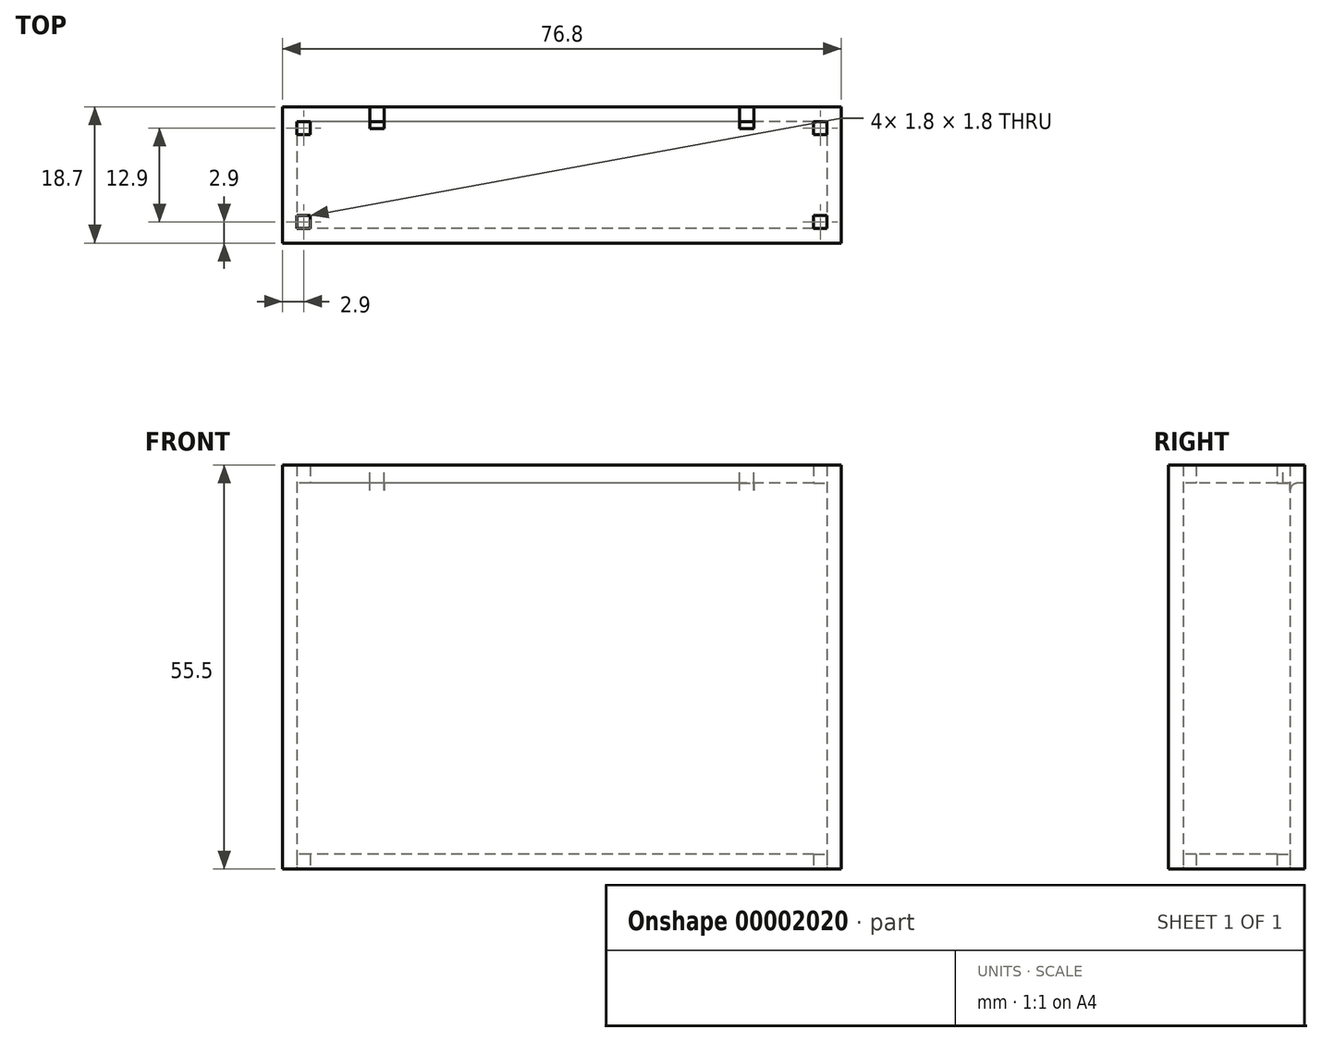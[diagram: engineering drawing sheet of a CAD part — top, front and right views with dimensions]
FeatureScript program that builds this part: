
annotation { "Feature Type Name" : "Feature", "Feature Type Description" : "" }
export const myFeature = defineFeature(function(context is Context, id is Id, definition is map)
    precondition{}
    {
        {
            var Q0;
            Q0=qCreatedBy(makeId("Top.planeOp"),FACE);
            var sketch = newSketch(context, id + "F0", { "sketchPlane" : qUnion([Q0])});
            skLineSegment(sketch, "E0.rect.bottom", {"start": v(36.4, 7.35) * mm, "end": v(-36.4, 7.35) * mm});
            skLineSegment(sketch, "E0.rect.top", {"start": v(36.4, -7.35) * mm, "end": v(-36.4, -7.35) * mm});
            skLineSegment(sketch, "E0.rect.left", {"start": v(36.4, 7.35) * mm, "end": v(36.4, -7.35) * mm});
            skLineSegment(sketch, "E0.rect.right", {"start": v(-36.4, 7.35) * mm, "end": v(-36.4, -7.35) * mm});
            skPoint(sketch, "E0.rect.middle", {"position": v(0, 0) * mm});
            skCircle(sketch, "E1", {"center": v(-29.15, 0.1) * mm, "radius": 7.25 * mm, "construction": true});
            skCircle(sketch, "E2", {"center": v(-14.65, -0.1) * mm, "radius": 7.25 * mm, "construction": true});
            skCircle(sketch, "E3", {"center": v(-0.15, 0.1) * mm, "radius": 7.25 * mm, "construction": true});
            skCircle(sketch, "E4", {"center": v(14.35, -0.1) * mm, "radius": 7.25 * mm, "construction": true});
            skCircle(sketch, "E5", {"center": v(28.84, 0.1) * mm, "radius": 7.25 * mm, "construction": true});
            skLineSegment(sketch, "E6.rect.bottom", {"start": v(38.4, 9.35) * mm, "end": v(-38.4, 9.35) * mm});
            skLineSegment(sketch, "E6.rect.top", {"start": v(38.4, -9.35) * mm, "end": v(-38.4, -9.35) * mm});
            skLineSegment(sketch, "E6.rect.left", {"start": v(38.4, 9.35) * mm, "end": v(38.4, -9.35) * mm});
            skLineSegment(sketch, "E6.rect.right", {"start": v(-38.4, 9.35) * mm, "end": v(-38.4, -9.35) * mm});
            skSolve(sketch);
        }
        {
            var Q0;
            Q0=makeQuery(id+"F0.imprint","IMPRINT",FACE,{"disambiguationData":[TD([[makeQuery(id+"F0.imprint","IMPRINT",EDGE,{"derivedFrom":sQuery(id+"F0.wireOp",EDGE,"E0.rect.bottom")}),-1.0]])]});
            extrude(context, id + "F1", {"entities" : qUnion([Q0]), "depth" : 54.5 * mm});
        }
        {
            var Q0;
            Q0=makeQuery(id+"F0.imprint","IMPRINT",FACE,{"disambiguationData":[TD([[makeQuery(id+"F0.imprint","IMPRINT",EDGE,{"derivedFrom":sQuery(id+"F0.wireOp",EDGE,"E0.rect.bottom")}),1.0]])]});
            extrude(context, id + "F2", {"entities" : qUnion([Q0]), "operationType" : NewBodyOperationType.ADD, "depth" : 2 * mm});
        }
        {
            var Q0;
            Q0=makeQuery(id+"F1.opExtrude","CAP_FACE",FACE,{"disambiguationData":[OSD([sQuery(id+"F0.wireOp",EDGE,"E0.rect.bottom"),sQuery(id+"F0.wireOp",EDGE,"E0.rect.top"),sQuery(id+"F0.wireOp",EDGE,"E0.rect.left"),sQuery(id+"F0.wireOp",EDGE,"E0.rect.right"),sQuery(id+"F0.wireOp",EDGE,"E6.rect.bottom"),sQuery(id+"F0.wireOp",EDGE,"E6.rect.top"),sQuery(id+"F0.wireOp",EDGE,"E6.rect.left"),sQuery(id+"F0.wireOp",EDGE,"E6.rect.right")])],"isStart":false});
            var sketch = newSketch(context, id + "F3", { "sketchPlane" : qUnion([Q0])});
            skLineSegment(sketch, "E7.0", {"start": v(38.4, 9.35) * mm, "end": v(-38.4, 9.35) * mm});
            skLineSegment(sketch, "E7.1", {"start": v(-38.4, 9.35) * mm, "end": v(-38.4, -9.35) * mm});
            skLineSegment(sketch, "E8.0", {"start": v(36.4, 7.35) * mm, "end": v(-36.4, 7.35) * mm});
            skLineSegment(sketch, "E8.1", {"start": v(-36.4, 7.35) * mm, "end": v(-36.4, -7.35) * mm});
            skLineSegment(sketch, "E8.2", {"start": v(36.4, -7.35) * mm, "end": v(-36.4, -7.35) * mm});
            skLineSegment(sketch, "E8.3", {"start": v(36.4, 7.35) * mm, "end": v(36.4, -7.35) * mm});
            skLineSegment(sketch, "E8.4", {"start": v(38.4, 9.35) * mm, "end": v(38.4, -9.35) * mm});
            skLineSegment(sketch, "E8.5", {"start": v(38.4, -9.35) * mm, "end": v(-38.4, -9.35) * mm});
            skSolve(sketch);
        }
        {
            var Q0;
            Q0=makeQuery(id+"F3.imprint","IMPRINT",FACE,{"disambiguationData":[TD([[makeQuery(id+"F3.imprint","IMPRINT",EDGE,{"derivedFrom":sQuery(id+"F3.wireOp",EDGE,"E8.0")}),1.0]])]});
            extrude(context, id + "F4", {"entities" : qUnion([Q0]), "oppositeDirection" : true, "depth" : 1.5 * mm});
        }
        {
            var Q0;
            Q0=makeQuery(id+"F1.opExtrude","CAP_FACE",FACE,{"disambiguationData":[OSD([sQuery(id+"F0.wireOp",EDGE,"E0.rect.bottom"),sQuery(id+"F0.wireOp",EDGE,"E0.rect.top"),sQuery(id+"F0.wireOp",EDGE,"E0.rect.left"),sQuery(id+"F0.wireOp",EDGE,"E0.rect.right"),sQuery(id+"F0.wireOp",EDGE,"E6.rect.bottom"),sQuery(id+"F0.wireOp",EDGE,"E6.rect.top"),sQuery(id+"F0.wireOp",EDGE,"E6.rect.left"),sQuery(id+"F0.wireOp",EDGE,"E6.rect.right")])],"isStart":false});
            var Q1;
            Q1=makeQuery(id+"F4.opExtrude","CAP_FACE",FACE,{"disambiguationData":[OSD([sQuery(id+"F3.wireOp",EDGE,"E8.0"),sQuery(id+"F3.wireOp",EDGE,"E8.1"),sQuery(id+"F3.wireOp",EDGE,"E8.2"),sQuery(id+"F3.wireOp",EDGE,"E8.3")])],"isStart":true});
            extrude(context, id + "F5", {"entities" : qUnion([Q0, Q1]), "operationType" : NewBodyOperationType.ADD, "depth" : 1 * mm});
        }
        {
            var Q0;
            Q0=makeQuery(id+"F4.opExtrude","CAP_FACE",FACE,{"disambiguationData":[OSD([sQuery(id+"F3.wireOp",EDGE,"E8.0"),sQuery(id+"F3.wireOp",EDGE,"E8.1"),sQuery(id+"F3.wireOp",EDGE,"E8.2"),sQuery(id+"F3.wireOp",EDGE,"E8.3")])],"isStart":false});
            var sketch = newSketch(context, id + "F6", { "sketchPlane" : qUnion([Q0])});
            skLineSegment(sketch, "E9.bottom", {"start": v(36.4, -7.35) * mm, "end": v(34.6, -7.35) * mm});
            skLineSegment(sketch, "E9.top", {"start": v(36.4, -5.55) * mm, "end": v(34.6, -5.55) * mm});
            skLineSegment(sketch, "E9.left", {"start": v(36.4, -7.35) * mm, "end": v(36.4, -5.55) * mm});
            skLineSegment(sketch, "E9.right", {"start": v(34.6, -7.35) * mm, "end": v(34.6, -5.55) * mm});
            skLineSegment(sketch, "E10.bottom", {"start": v(36.4, 7.35) * mm, "end": v(34.6, 7.35) * mm});
            skLineSegment(sketch, "E10.top", {"start": v(36.4, 5.55) * mm, "end": v(34.6, 5.55) * mm});
            skLineSegment(sketch, "E10.left", {"start": v(36.4, 7.35) * mm, "end": v(36.4, 5.55) * mm});
            skLineSegment(sketch, "E10.right", {"start": v(34.6, 7.35) * mm, "end": v(34.6, 5.55) * mm});
            skLineSegment(sketch, "E11.bottom", {"start": v(-36.4, -7.35) * mm, "end": v(-34.6, -7.35) * mm});
            skLineSegment(sketch, "E11.top", {"start": v(-36.4, -5.55) * mm, "end": v(-34.6, -5.55) * mm});
            skLineSegment(sketch, "E11.left", {"start": v(-36.4, -7.35) * mm, "end": v(-36.4, -5.55) * mm});
            skLineSegment(sketch, "E11.right", {"start": v(-34.6, -7.35) * mm, "end": v(-34.6, -5.55) * mm});
            skLineSegment(sketch, "E12.bottom", {"start": v(-36.4, 7.35) * mm, "end": v(-34.6, 7.35) * mm});
            skLineSegment(sketch, "E12.top", {"start": v(-36.4, 5.55) * mm, "end": v(-34.6, 5.55) * mm});
            skLineSegment(sketch, "E12.left", {"start": v(-36.4, 7.35) * mm, "end": v(-36.4, 5.55) * mm});
            skLineSegment(sketch, "E12.right", {"start": v(-34.6, 7.35) * mm, "end": v(-34.6, 5.55) * mm});
            skSolve(sketch);
        }
        {
            var Q0;
            Q0=makeQuery(id+"F6.imprint","IMPRINT",FACE,{"disambiguationData":[TD([[makeQuery(id+"F6.imprint","IMPRINT",EDGE,{"derivedFrom":sQuery(id+"F6.wireOp",EDGE,"E9.bottom")}),-1.0]])]});
            var Q1;
            Q1=makeQuery(id+"F6.imprint","IMPRINT",FACE,{"disambiguationData":[TD([[makeQuery(id+"F6.imprint","IMPRINT",EDGE,{"derivedFrom":sQuery(id+"F6.wireOp",EDGE,"E10.bottom")}),1.0]])]});
            var Q2;
            Q2=makeQuery(id+"F6.imprint","IMPRINT",FACE,{"disambiguationData":[TD([[makeQuery(id+"F6.imprint","IMPRINT",EDGE,{"derivedFrom":sQuery(id+"F6.wireOp",EDGE,"E11.bottom")}),-1.0]])]});
            var Q3;
            Q3=makeQuery(id+"F6.imprint","IMPRINT",FACE,{"disambiguationData":[TD([[makeQuery(id+"F6.imprint","IMPRINT",EDGE,{"derivedFrom":sQuery(id+"F6.wireOp",EDGE,"E12.bottom")}),1.0]])]});
            extrude(context, id + "F7", {"entities" : qUnion([Q0, Q1, Q2, Q3]), "operationType" : NewBodyOperationType.REMOVE, "endBound" : BoundingType.SYMMETRIC, "oppositeDirection" : true, "depth" : 300 * mm});
        }
        {
            var Q0;
            Q0=makeQuery(id+"F5.boolean.opBoolean","MERGE",FACE,{"derivedFrom":[makeQuery(id+"F5.opExtrude","CAP_FACE",FACE,{"disambiguationData":[OSD([sQuery(id+"F0.wireOp",EDGE,"E0.rect.bottom"),sQuery(id+"F0.wireOp",EDGE,"E0.rect.top"),sQuery(id+"F0.wireOp",EDGE,"E0.rect.left"),sQuery(id+"F0.wireOp",EDGE,"E0.rect.right"),sQuery(id+"F0.wireOp",EDGE,"E6.rect.bottom"),sQuery(id+"F0.wireOp",EDGE,"E6.rect.top"),sQuery(id+"F0.wireOp",EDGE,"E6.rect.left"),sQuery(id+"F0.wireOp",EDGE,"E6.rect.right")])],"isStart":false}),makeQuery(id+"F5.opExtrude","CAP_FACE",FACE,{"disambiguationData":[OSD([sQuery(id+"F3.wireOp",EDGE,"E8.0"),sQuery(id+"F3.wireOp",EDGE,"E8.1"),sQuery(id+"F3.wireOp",EDGE,"E8.2"),sQuery(id+"F3.wireOp",EDGE,"E8.3")])],"isStart":false})]});
            var sketch = newSketch(context, id + "F8", { "sketchPlane" : qUnion([Q0])});
            skLineSegment(sketch, "E13.bottom", {"start": v(-24.4, 9.35) * mm, "end": v(-26.4, 9.35) * mm});
            skLineSegment(sketch, "E13.top", {"start": v(-24.4, 6.35) * mm, "end": v(-26.4, 6.35) * mm});
            skLineSegment(sketch, "E13.left", {"start": v(-24.4, 9.35) * mm, "end": v(-24.4, 6.35) * mm});
            skLineSegment(sketch, "E13.right", {"start": v(-26.4, 9.35) * mm, "end": v(-26.4, 6.35) * mm});
            skLineSegment(sketch, "E14.bottom", {"start": v(24.4, 9.35) * mm, "end": v(26.4, 9.35) * mm});
            skLineSegment(sketch, "E14.top", {"start": v(24.4, 6.35) * mm, "end": v(26.4, 6.35) * mm});
            skLineSegment(sketch, "E14.left", {"start": v(24.4, 9.35) * mm, "end": v(24.4, 6.35) * mm});
            skLineSegment(sketch, "E14.right", {"start": v(26.4, 9.35) * mm, "end": v(26.4, 6.35) * mm});
            skPoint(sketch, "E15", {"position": v(0, 9.35) * mm});
            skSolve(sketch);
        }
        {
            var Q0;
            Q0=makeQuery(id+"F8.imprint","IMPRINT",FACE,{"disambiguationData":[TD([[makeQuery(id+"F8.imprint","IMPRINT",EDGE,{"derivedFrom":sQuery(id+"F8.wireOp",EDGE,"E13.bottom")}),1.0]])]});
            var Q1;
            Q1=makeQuery(id+"F8.imprint","IMPRINT",FACE,{"disambiguationData":[TD([[makeQuery(id+"F8.imprint","IMPRINT",EDGE,{"derivedFrom":sQuery(id+"F8.wireOp",EDGE,"E14.bottom")}),1.0]])]});
            extrude(context, id + "F9", {"entities" : qUnion([Q0, Q1]), "operationType" : NewBodyOperationType.REMOVE, "oppositeDirection" : true, "depth" : 2.5 * mm});
        }
        {
            var Q0;
            Q0=makeQuery(id+"F9.boolean.opBoolean","INTERSECT",EDGE,{"derivedFrom":[makeQuery(id+"F7.boolean.opBoolean","MERGE",FACE,{"derivedFrom":[makeQuery(id+"F1.opExtrude","SWEPT_FACE",FACE,{"disambiguationData":[OSD([sQuery(id+"F0.wireOp",EDGE,"E0.rect.bottom")])]}),makeQuery(id+"F7.opExtrude","SWEPT_FACE",FACE,{"disambiguationData":[OSD([sQuery(id+"F6.wireOp",EDGE,"E9.bottom")])]}),makeQuery(id+"F7.opExtrude","SWEPT_FACE",FACE,{"disambiguationData":[OSD([sQuery(id+"F6.wireOp",EDGE,"E11.bottom")])]})]}),makeQuery(id+"F9.opExtrude","CAP_FACE",FACE,{"disambiguationData":[OSD([sQuery(id+"F8.wireOp",EDGE,"E13.bottom"),sQuery(id+"F8.wireOp",EDGE,"E13.top"),sQuery(id+"F8.wireOp",EDGE,"E13.left"),sQuery(id+"F8.wireOp",EDGE,"E13.right")])],"isStart":false})]});
            var Q1;
            Q1=makeQuery(id+"F9.boolean.opBoolean","COPY",EDGE,{"derivedFrom":makeQuery(id+"F9.opExtrude","CAP_EDGE",EDGE,{"disambiguationData":[OSD([sQuery(id+"F8.wireOp",EDGE,"E13.top")])],"isStart":false})});
            var Q2;
            Q2=makeQuery(id+"F9.boolean.opBoolean","COPY",EDGE,{"derivedFrom":makeQuery(id+"F9.opExtrude","CAP_EDGE",EDGE,{"disambiguationData":[OSD([sQuery(id+"F8.wireOp",EDGE,"E14.top")])],"isStart":false})});
            var Q3;
            Q3=makeQuery(id+"F9.boolean.opBoolean","INTERSECT",EDGE,{"derivedFrom":[makeQuery(id+"F7.boolean.opBoolean","MERGE",FACE,{"derivedFrom":[makeQuery(id+"F1.opExtrude","SWEPT_FACE",FACE,{"disambiguationData":[OSD([sQuery(id+"F0.wireOp",EDGE,"E0.rect.bottom")])]}),makeQuery(id+"F7.opExtrude","SWEPT_FACE",FACE,{"disambiguationData":[OSD([sQuery(id+"F6.wireOp",EDGE,"E9.bottom")])]}),makeQuery(id+"F7.opExtrude","SWEPT_FACE",FACE,{"disambiguationData":[OSD([sQuery(id+"F6.wireOp",EDGE,"E11.bottom")])]})]}),makeQuery(id+"F9.opExtrude","CAP_FACE",FACE,{"disambiguationData":[OSD([sQuery(id+"F8.wireOp",EDGE,"E14.bottom"),sQuery(id+"F8.wireOp",EDGE,"E14.top"),sQuery(id+"F8.wireOp",EDGE,"E14.left"),sQuery(id+"F8.wireOp",EDGE,"E14.right")])],"isStart":false})]});
            fillet(context, id + "F10", {"entities" : qUnion([Q0, Q1, Q2, Q3]), "radius" : 1 * mm, "tangentPropagation" : true, "allowEdgeOverflow" : false});
        }
    });
